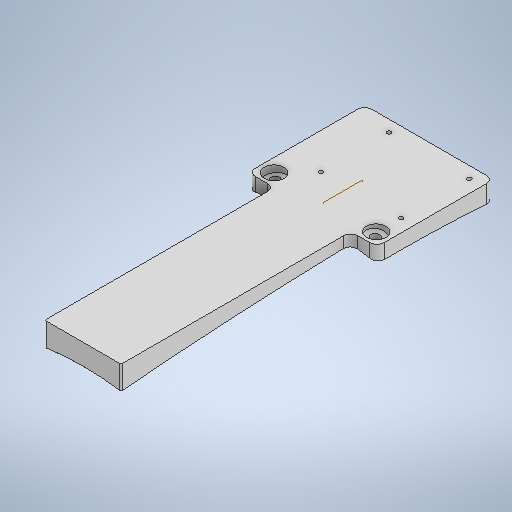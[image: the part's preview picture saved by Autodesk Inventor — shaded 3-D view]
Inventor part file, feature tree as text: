
AUTODESK INVENTOR PART (.ipt)
format: ipt  version: 2025 (Build 290162000, 162)  size: 570,368 bytes
history: native  units: in
note: dims shown in document units (in); Inventor stores cm internally (conversion verified against a paired STEP export)
features: sketch x13, extrude x10, other x4, mirror x2, loft x2, fillet x2, revolve x1, plane x1
ambient origin geometry x8: Origin, YZ Plane, XZ Plane, XY Plane, X Axis, Y Axis, Z Axis, Center Point
bodies: Solid1 (feature_tree)
feature tree (35):
  extrude  "Extrusion1"  Depth=1.5in
  revolve  "Revolution1"  [1 undecoded]
  extrude  "Extrusion2"  Depth=0.0563in
  plane  "Work Plane9"
  mirror  "Mirror1"
  extrude  "Extrusion3"  TaperAngle=90.0deg  [1 undecoded]
  mirror  "Mirror2"
  extrude  "Extrusion4"  TaperAngle=90.0deg  [1 undecoded]
  extrude  "Extrusion5"  Depth=0.6748in
  extrude  "Extrusion13"  TaperAngle=180.0deg  [1 undecoded]
  loft  "Loft4"
  extrude  "Extrusion14"  Depth=0.356in
  extrude  "Extrusion15"  Depth=0.712in
  extrude  "Extrusion16"  Depth=2.585in
  loft  "Loft5"
  fillet  "Fillet4"  Radius=0.33in
  fillet  "Fillet5"  Radius=0.11in
  extrude  "Extrusion17"  Depth=1.93in
  sketch  "Sketch1"  dims[d2=0.25in d3=1.5in]
  sketch  "Sketch2"  dims[d4=1.0in d5=0.0in d6=0.1in]
  sketch  "Sketch3"  dims[d7=0.12in d8=0.0563in]
  sketch  "Sketch5"  dims[d9=0.2in d10=90.0deg]
  sketch  "Sketch6"  dims[d11=0.275in d12=90.0deg]
  sketch  "Sketch7"  dims[d13=0.15in d14=0.6748in]
  sketch  "Sketch8"  dims[d15=0.1in d16=180.0deg]
  sketch  "Sketch19"  dims[d17=1.0in d18=0.0in d27=-1.8228in]
  other  "Edges7"
  other  "Edges8"
  sketch  "Sketch20"  dims[d28=1.0in d29=0.0in d30=0.356in]
  sketch  "Sketch21"  dims[d31=90.0deg d32=0.712in]
  sketch  "Sketch22"  dims[d33=1.0in d34=0.0in d52=2.585in]
  sketch  "Sketch23"  dims[d53=2.585in d54=0.36in d55=0.33in d56=0.11in]
  other  "Edges9"
  other  "Edges10"
  sketch  "Sketch24"  dims[d57=2.27in d58=1.93in d59=0.11in d60=0.11in d61=0.11in d62=0.2in d63=0.0in d64=0.345in d65=0.099in d66=0.099in d76=0.11in d113=0.01in d114=0.01in d115=0.01in d116=0.001in d117=0.0in d118=29.638in d119=0.0in d120=90.0deg d121=0.0in d122=90.0deg d123=0.0in d124=90.0deg d125=6.5in d126=1.08in d127=1.08in d128=0.1in d129=0.0in d130=0.51in d131=0.08in d132=0.08in d133=0.075in d134=0.075in d135=0.075in d136=90.0deg d137=0.001in d138=0.0in d139=0.001in d140=0.0in d141=100.0in d142=0.0in d143=90.0deg d144=0.0in d145=90.0deg d146=0.0in d147=90.0deg d148=0.05in d149=0.2in d150=0.113in d151=0.113in d152=0.113in d153=0.113in d154=10.0in d155=0.0in d95=0.5in d96=0.0344in d97=0.5in d98=0.0344in]
note: 4 required parameter values undecoded (feature->parameter linkage not recoverable at this tier; creation-order binding heuristic only, values carry confidence <= 0.55)